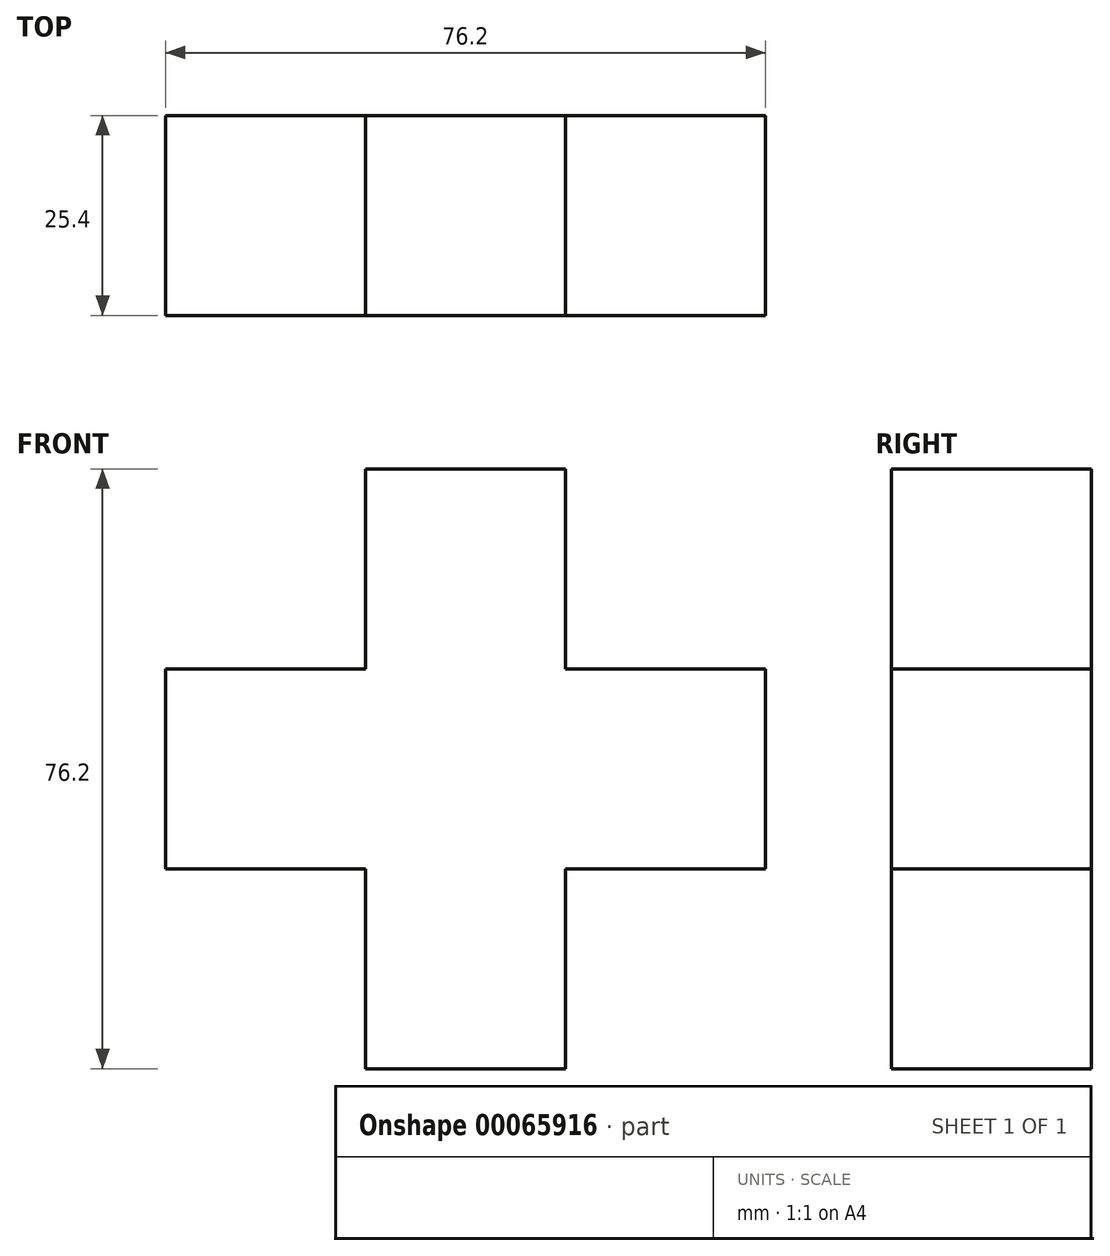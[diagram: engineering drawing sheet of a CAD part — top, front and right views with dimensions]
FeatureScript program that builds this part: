
annotation { "Feature Type Name" : "Feature", "Feature Type Description" : "" }
export const myFeature = defineFeature(function(context is Context, id is Id, definition is map)
    precondition{}
    {
        {
            var Q0;
            Q0=qCreatedBy(makeId("Front.planeOp"),FACE);
            var sketch = newSketch(context, id + "F0", { "sketchPlane" : qUnion([Q0])});
            skLineSegment(sketch, "E0.bottom", {"start": v(0, 0) * mm, "end": v(25.4, 0) * mm});
            skLineSegment(sketch, "E0.top", {"start": v(0, 25.4) * mm, "end": v(25.4, 25.4) * mm});
            skLineSegment(sketch, "E0.left", {"start": v(0, 0) * mm, "end": v(0, 25.4) * mm});
            skLineSegment(sketch, "E0.right", {"start": v(25.4, 0) * mm, "end": v(25.4, 25.4) * mm});
            skSolve(sketch);
        }
        {
            var Q0;
            Q0 = qSketchRegion(id + "F0", true);
            extrude(context, id + "F1", {"entities" : qUnion([Q0]), "endBound" : BoundingType.SYMMETRIC, "depth" : 25.4 * mm});
        }
        {
            var Q0;
            Q0=makeQuery(id+"F1.opExtrude","SWEPT_FACE",FACE,{"disambiguationData":[OSD([sQuery(id+"F0.wireOp",EDGE,"E0.top")])]});
            var sketch = newSketch(context, id + "F2", { "sketchPlane" : qUnion([Q0])});
            skLineSegment(sketch, "E1.bottom", {"start": v(0, -12.7) * mm, "end": v(25.4, -12.7) * mm});
            skLineSegment(sketch, "E1.top", {"start": v(0, 12.7) * mm, "end": v(25.4, 12.7) * mm});
            skLineSegment(sketch, "E1.left", {"start": v(0, -12.7) * mm, "end": v(0, 12.7) * mm});
            skLineSegment(sketch, "E1.right", {"start": v(25.4, -12.7) * mm, "end": v(25.4, 12.7) * mm});
            skSolve(sketch);
        }
        {
            var Q0;
            Q0 = qSketchRegion(id + "F2", true);
            extrude(context, id + "F3", {"entities" : qUnion([Q0]), "operationType" : NewBodyOperationType.ADD, "depth" : 25.4 * mm});
        }
        {
            var Q0;
            Q0=makeQuery(id+"F3.boolean.opBoolean","MERGE",FACE,{"derivedFrom":[makeQuery(id+"F1.opExtrude","SWEPT_FACE",FACE,{"disambiguationData":[OSD([sQuery(id+"F0.wireOp",EDGE,"E0.left")])]}),makeQuery(id+"F3.opExtrude","SWEPT_FACE",FACE,{"disambiguationData":[OSD([sQuery(id+"F2.wireOp",EDGE,"E1.left")])]})]});
            var sketch = newSketch(context, id + "F4", { "sketchPlane" : qUnion([Q0])});
            skLineSegment(sketch, "E2.bottom", {"start": v(-12.7, 0) * mm, "end": v(12.7, 0) * mm});
            skLineSegment(sketch, "E2.top", {"start": v(-12.7, 25.4) * mm, "end": v(12.7, 25.4) * mm});
            skLineSegment(sketch, "E2.left", {"start": v(-12.7, 0) * mm, "end": v(-12.7, 25.4) * mm});
            skLineSegment(sketch, "E2.right", {"start": v(12.7, 0) * mm, "end": v(12.7, 25.4) * mm});
            skSolve(sketch);
        }
        {
            var Q0;
            Q0 = qSketchRegion(id + "F4", true);
            extrude(context, id + "F5", {"entities" : qUnion([Q0]), "operationType" : NewBodyOperationType.ADD, "depth" : 25.4 * mm});
        }
        {
            var Q0;
            Q0=makeQuery(id+"F3.boolean.opBoolean","MERGE",FACE,{"derivedFrom":[makeQuery(id+"F1.opExtrude","SWEPT_FACE",FACE,{"disambiguationData":[OSD([sQuery(id+"F0.wireOp",EDGE,"E0.right")])]}),makeQuery(id+"F3.opExtrude","SWEPT_FACE",FACE,{"disambiguationData":[OSD([sQuery(id+"F2.wireOp",EDGE,"E1.right")])]})]});
            var sketch = newSketch(context, id + "F6", { "sketchPlane" : qUnion([Q0])});
            skLineSegment(sketch, "E3.bottom", {"start": v(12.7, 0) * mm, "end": v(-12.7, 0) * mm});
            skLineSegment(sketch, "E3.top", {"start": v(12.7, 25.4) * mm, "end": v(-12.7, 25.4) * mm});
            skLineSegment(sketch, "E3.left", {"start": v(12.7, 0) * mm, "end": v(12.7, 25.4) * mm});
            skLineSegment(sketch, "E3.right", {"start": v(-12.7, 0) * mm, "end": v(-12.7, 25.4) * mm});
            skSolve(sketch);
        }
        {
            var Q0;
            Q0 = qSketchRegion(id + "F6", true);
            extrude(context, id + "F7", {"entities" : qUnion([Q0]), "operationType" : NewBodyOperationType.ADD, "depth" : 25.4 * mm});
        }
        {
            var Q0;
            Q0=makeQuery(id+"F7.boolean.opBoolean","MERGE",FACE,{"derivedFrom":[makeQuery(id+"F5.boolean.opBoolean","MERGE",FACE,{"derivedFrom":[makeQuery(id+"F1.opExtrude","SWEPT_FACE",FACE,{"disambiguationData":[OSD([sQuery(id+"F0.wireOp",EDGE,"E0.bottom")])]}),makeQuery(id+"F5.opExtrude","SWEPT_FACE",FACE,{"disambiguationData":[OSD([sQuery(id+"F4.wireOp",EDGE,"E2.bottom")])]})]}),makeQuery(id+"F7.opExtrude","SWEPT_FACE",FACE,{"disambiguationData":[OSD([sQuery(id+"F6.wireOp",EDGE,"E3.bottom")])]})]});
            var sketch = newSketch(context, id + "F8", { "sketchPlane" : qUnion([Q0])});
            skLineSegment(sketch, "E4.bottom", {"start": v(0, -12.7) * mm, "end": v(25.4, -12.7) * mm});
            skLineSegment(sketch, "E4.top", {"start": v(0, 12.7) * mm, "end": v(25.4, 12.7) * mm});
            skLineSegment(sketch, "E4.left", {"start": v(0, -12.7) * mm, "end": v(0, 12.7) * mm});
            skLineSegment(sketch, "E4.right", {"start": v(25.4, -12.7) * mm, "end": v(25.4, 12.7) * mm});
            skSolve(sketch);
        }
        {
            var Q0;
            Q0 = qSketchRegion(id + "F8", true);
            extrude(context, id + "F9", {"entities" : qUnion([Q0]), "operationType" : NewBodyOperationType.ADD, "depth" : 25.4 * mm});
        }
    });
